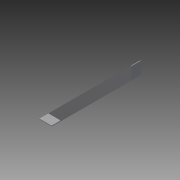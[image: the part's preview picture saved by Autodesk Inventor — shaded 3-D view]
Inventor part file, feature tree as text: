
AUTODESK INVENTOR PART (.ipt)
format: ipt  version: 2012 (Build 160160000, 160)  size: 90,112 bytes
history: native  units: in
note: dims shown in document units (in); Inventor stores cm internally (conversion verified against a paired STEP export)
features: extrude x2, sketch x1
ambient origin geometry x8: Origin, YZ Plane, XZ Plane, XY Plane, X Axis, Y Axis, Z Axis, Center Point
bodies: Solid1 (feature_tree)
feature tree (3):
  sketch  "Sketch1"  dims[d0=1.0in d1=135.0deg d2=0.0625in d3=0.0625in d4=0.0438in d5=0.0625in d6=0.0625in d7=10.0in d9=0.0438in d10=0.0625in d11=0.0625in d12=0.0in d13=1.0in d14=0.0in]
  extrude  "Extrusion1"  TaperAngle=135.0deg  [1 undecoded]
  extrude  "Extrusion2"  Depth=0.0625in
note: 1 required parameter value undecoded (feature->parameter linkage not recoverable at this tier; creation-order binding heuristic only, values carry confidence <= 0.55)
